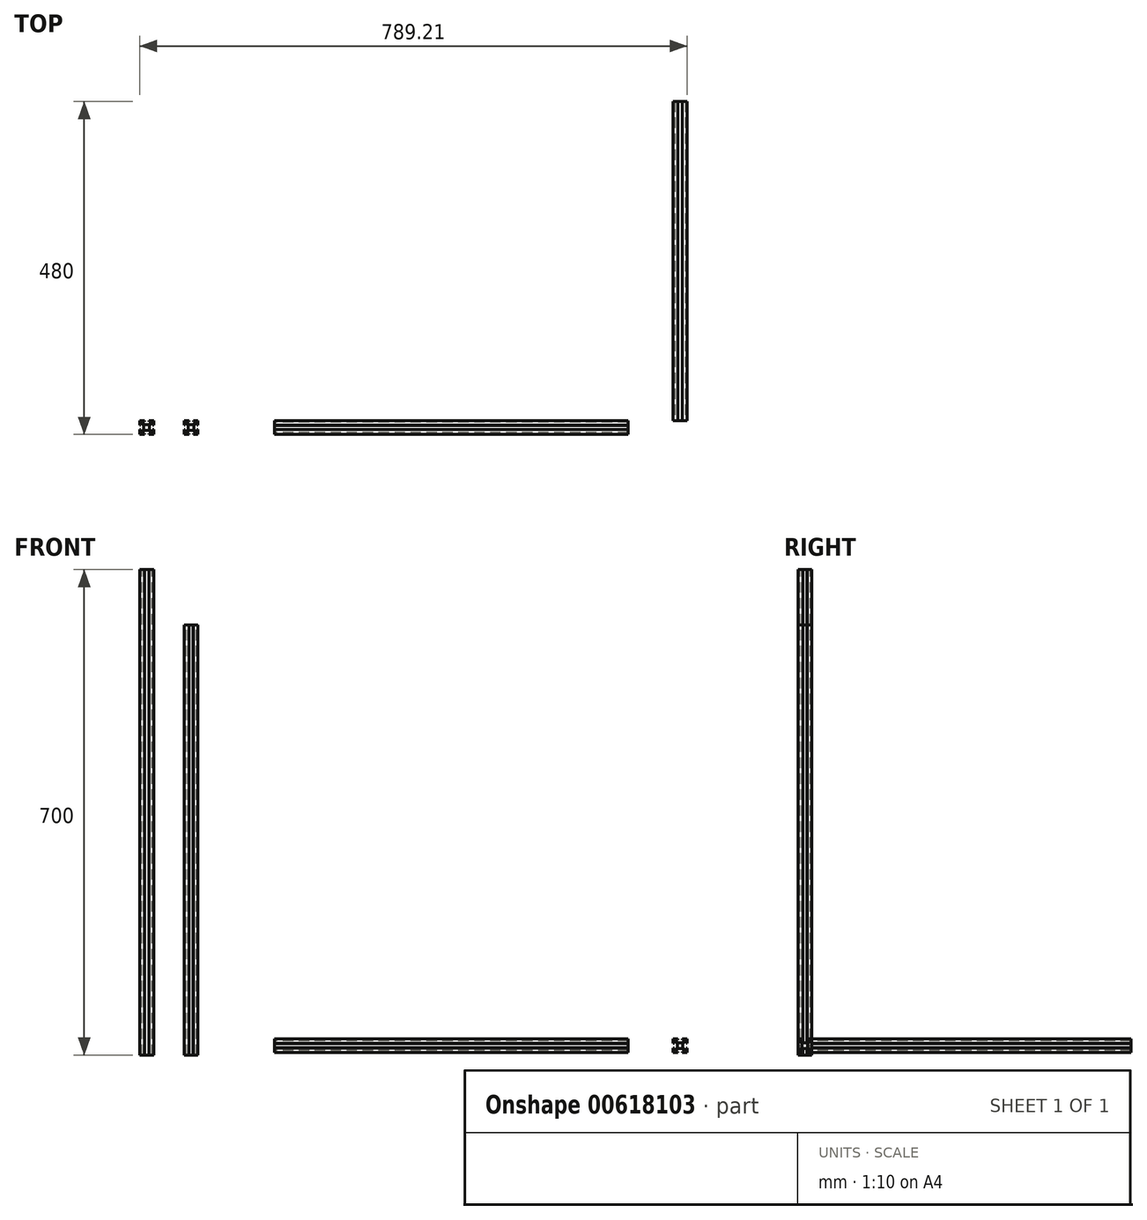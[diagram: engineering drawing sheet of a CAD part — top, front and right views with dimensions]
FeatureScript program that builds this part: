
annotation { "Feature Type Name" : "Feature", "Feature Type Description" : "" }
export const myFeature = defineFeature(function(context is Context, id is Id, definition is map)
    precondition{}
    {
        {
            var Q0;
            Q0=qCreatedBy(makeId("Front.planeOp"),FACE);
            var sketch = newSketch(context, id + "F0", { "sketchPlane" : qUnion([Q0])});
            skLineSegment(sketch, "E0.bottom", {"start": v(-64.1, 630.58) * mm, "end": v(-44.1, 630.58) * mm});
            skLineSegment(sketch, "E0.top", {"start": v(-64.1, -69.42) * mm, "end": v(-44.1, -69.42) * mm});
            skLineSegment(sketch, "E0.left", {"start": v(-64.1, 630.58) * mm, "end": v(-64.1, -69.42) * mm});
            skLineSegment(sketch, "E0.right", {"start": v(-44.1, 630.58) * mm, "end": v(-44.1, -69.42) * mm});
            skLineSegment(sketch, "E1.bottom", {"start": v(130.25, -46.02) * mm, "end": v(640.25, -46.02) * mm});
            skLineSegment(sketch, "E1.top", {"start": v(130.25, -66.02) * mm, "end": v(640.25, -66.02) * mm});
            skLineSegment(sketch, "E1.left", {"start": v(130.25, -46.02) * mm, "end": v(130.25, -66.02) * mm});
            skLineSegment(sketch, "E1.right", {"start": v(640.25, -46.02) * mm, "end": v(640.25, -66.02) * mm});
            skLineSegment(sketch, "E2.bottom", {"start": v(705.1, -66.02) * mm, "end": v(725.1, -66.02) * mm});
            skLineSegment(sketch, "E2.top", {"start": v(705.1, -46.02) * mm, "end": v(725.1, -46.02) * mm});
            skLineSegment(sketch, "E2.left", {"start": v(705.1, -66.02) * mm, "end": v(705.1, -46.02) * mm});
            skLineSegment(sketch, "E2.right", {"start": v(725.1, -66.02) * mm, "end": v(725.1, -46.02) * mm});
            skLineSegment(sketch, "E3.bottom", {"start": v(0, -69.42) * mm, "end": v(20, -69.42) * mm});
            skLineSegment(sketch, "E3.top", {"start": v(0, 550.58) * mm, "end": v(20, 550.58) * mm});
            skLineSegment(sketch, "E3.left", {"start": v(0, -69.42) * mm, "end": v(0, 550.58) * mm});
            skLineSegment(sketch, "E3.right", {"start": v(20, -69.42) * mm, "end": v(20, 550.58) * mm});
            skLineSegment(sketch, "E4.bottom", {"start": v(705.1, -46.02) * mm, "end": v(711.9, -46.02) * mm});
            skLineSegment(sketch, "E4.top", {"start": v(711.1, -56.02) * mm, "end": v(715.1, -56.02) * mm, "construction": true});
            skLineSegment(sketch, "E4.left", {"start": v(705.1, -46.02) * mm, "end": v(705.1, -52.82) * mm});
            skLineSegment(sketch, "E4.right", {"start": v(715.1, -52.02) * mm, "end": v(715.1, -56.02) * mm, "construction": true});
            skLineSegment(sketch, "E5", {"start": v(706.5, -48.41) * mm, "end": v(706.5, -52.82) * mm});
            skLineSegment(sketch, "E6", {"start": v(706.5, -52.82) * mm, "end": v(705.1, -52.82) * mm});
            skLineSegment(sketch, "E7", {"start": v(707.49, -47.42) * mm, "end": v(711.9, -47.42) * mm});
            skLineSegment(sketch, "E8", {"start": v(711.9, -47.42) * mm, "end": v(711.9, -46.02) * mm});
            skLineSegment(sketch, "E9", {"start": v(705.1, -46.02) * mm, "end": v(715.1, -56.02) * mm, "construction": true});
            skLineSegment(sketch, "E10", {"start": v(711.1, -53.01) * mm, "end": v(706.5, -48.41) * mm});
            skLineSegment(sketch, "E11", {"start": v(707.49, -47.42) * mm, "end": v(712.09, -52.02) * mm});
            skLineSegment(sketch, "E12", {"start": v(712.09, -52.02) * mm, "end": v(715.1, -52.02) * mm});
            skLineSegment(sketch, "E13", {"start": v(711.1, -53.01) * mm, "end": v(711.1, -56.02) * mm});
            skLineSegment(sketch, "E14.MirrorCS", {"start": v(722.7, -47.42) * mm, "end": v(718.1, -52.02) * mm});
            skLineSegment(sketch, "E15.MirrorCS", {"start": v(718.1, -52.02) * mm, "end": v(715.1, -52.02) * mm});
            skLineSegment(sketch, "E16.MirrorCS", {"start": v(719.1, -53.01) * mm, "end": v(719.1, -56.02) * mm});
            skLineSegment(sketch, "E17.MirrorCS", {"start": v(725.1, -46.02) * mm, "end": v(715.1, -56.02) * mm, "construction": true});
            skLineSegment(sketch, "E18.MirrorCS", {"start": v(719.1, -56.02) * mm, "end": v(715.1, -56.02) * mm, "construction": true});
            skLineSegment(sketch, "E19.MirrorCS", {"start": v(718.3, -47.42) * mm, "end": v(718.3, -46.02) * mm});
            skLineSegment(sketch, "E20.MirrorCS", {"start": v(719.1, -53.01) * mm, "end": v(723.7, -48.41) * mm});
            skLineSegment(sketch, "E21.MirrorCS", {"start": v(725.1, -46.02) * mm, "end": v(725.1, -52.82) * mm});
            skLineSegment(sketch, "E22.MirrorCS", {"start": v(723.7, -52.82) * mm, "end": v(725.1, -52.82) * mm});
            skLineSegment(sketch, "E23.MirrorCS", {"start": v(723.7, -48.41) * mm, "end": v(723.7, -52.82) * mm});
            skLineSegment(sketch, "E24.MirrorCS", {"start": v(725.1, -46.02) * mm, "end": v(718.3, -46.02) * mm});
            skLineSegment(sketch, "E25.MirrorCS", {"start": v(722.7, -47.42) * mm, "end": v(718.3, -47.42) * mm});
            skLineSegment(sketch, "E26.MirrorCS", {"start": v(725.1, -66.02) * mm, "end": v(725.1, -59.22) * mm});
            skLineSegment(sketch, "E27.MirrorCS", {"start": v(706.5, -63.63) * mm, "end": v(706.5, -59.22) * mm});
            skLineSegment(sketch, "E28.MirrorCS", {"start": v(711.1, -59.03) * mm, "end": v(711.1, -56.02) * mm});
            skLineSegment(sketch, "E29.MirrorCS", {"start": v(715.1, -60.02) * mm, "end": v(715.1, -56.02) * mm, "construction": true});
            skLineSegment(sketch, "E30.MirrorCS", {"start": v(723.7, -63.63) * mm, "end": v(723.7, -59.22) * mm});
            skLineSegment(sketch, "E31.MirrorCS", {"start": v(718.1, -60.02) * mm, "end": v(715.1, -60.02) * mm});
            skLineSegment(sketch, "E32.MirrorCS", {"start": v(718.3, -64.62) * mm, "end": v(718.3, -66.02) * mm});
            skLineSegment(sketch, "E33.MirrorCS", {"start": v(719.1, -59.03) * mm, "end": v(723.7, -63.63) * mm});
            skLineSegment(sketch, "E34.MirrorCS", {"start": v(705.1, -66.02) * mm, "end": v(715.1, -56.02) * mm, "construction": true});
            skLineSegment(sketch, "E35.MirrorCS", {"start": v(707.49, -64.62) * mm, "end": v(711.9, -64.62) * mm});
            skLineSegment(sketch, "E36.MirrorCS", {"start": v(722.7, -64.62) * mm, "end": v(718.3, -64.62) * mm});
            skLineSegment(sketch, "E37.MirrorCS", {"start": v(706.5, -59.22) * mm, "end": v(705.1, -59.22) * mm});
            skLineSegment(sketch, "E38.MirrorCS", {"start": v(705.1, -66.02) * mm, "end": v(711.9, -66.02) * mm});
            skLineSegment(sketch, "E39.MirrorCS", {"start": v(719.1, -59.03) * mm, "end": v(719.1, -56.02) * mm});
            skLineSegment(sketch, "E40.MirrorCS", {"start": v(707.49, -64.62) * mm, "end": v(712.09, -60.02) * mm});
            skLineSegment(sketch, "E41.MirrorCS", {"start": v(712.09, -60.02) * mm, "end": v(715.1, -60.02) * mm});
            skLineSegment(sketch, "E42.MirrorCS", {"start": v(705.1, -66.02) * mm, "end": v(705.1, -59.22) * mm});
            skLineSegment(sketch, "E43.MirrorCS", {"start": v(711.1, -59.03) * mm, "end": v(706.5, -63.63) * mm});
            skLineSegment(sketch, "E44.MirrorCS", {"start": v(725.1, -66.02) * mm, "end": v(715.1, -56.02) * mm, "construction": true});
            skLineSegment(sketch, "E45.MirrorCS", {"start": v(723.7, -59.22) * mm, "end": v(725.1, -59.22) * mm});
            skLineSegment(sketch, "E46.MirrorCS", {"start": v(722.7, -64.62) * mm, "end": v(718.1, -60.02) * mm});
            skLineSegment(sketch, "E47.MirrorCS", {"start": v(725.1, -66.02) * mm, "end": v(718.3, -66.02) * mm});
            skLineSegment(sketch, "E48.MirrorCS", {"start": v(711.9, -64.62) * mm, "end": v(711.9, -66.02) * mm});
            skLineSegment(sketch, "E49", {"start": v(711.9, -46.02) * mm, "end": v(718.3, -46.02) * mm});
            skLineSegment(sketch, "E50", {"start": v(725.1, -52.82) * mm, "end": v(725.1, -59.22) * mm});
            skLineSegment(sketch, "E51", {"start": v(718.3, -66.02) * mm, "end": v(711.9, -66.02) * mm});
            skLineSegment(sketch, "E52", {"start": v(705.1, -59.22) * mm, "end": v(705.1, -52.82) * mm});
            skSolve(sketch);
        }
        {
            var Q0;
            Q0=makeQuery(id+"F0.imprint","IMPRINT",FACE,{"disambiguationData":[TD([[makeQuery(id+"F0.imprint","IMPRINT",EDGE,{"derivedFrom":sQuery(id+"F0.wireOp",EDGE,"E0.bottom")}),-1.0]])]});
            var Q1;
            Q1=makeQuery(id+"F0.imprint","IMPRINT",FACE,{"disambiguationData":[TD([[makeQuery(id+"F0.imprint","IMPRINT",EDGE,{"derivedFrom":sQuery(id+"F0.wireOp",EDGE,"E1.bottom")}),-1.0]])]});
            var Q2;
            Q2=makeQuery(id+"F0.imprint","IMPRINT",FACE,{"disambiguationData":[TD([[makeQuery(id+"F0.imprint","IMPRINT",EDGE,{"derivedFrom":sQuery(id+"F0.wireOp",EDGE,"E3.bottom")}),1.0]])]});
            var Q3;
            Q3=makeQuery(id+"F0.imprint","IMPRINT",FACE,{"disambiguationData":[TD([[makeQuery(id+"F0.imprint","IMPRINT",EDGE,{"derivedFrom":sQuery(id+"F0.wireOp",EDGE,"fPh9Yb10-BMAz-MM7O-woml-nyBZ1UUOM5pv.bottom")}),-1.0]])]});
            extrude(context, id + "F1", {"entities" : qUnion([Q0, Q1, Q2, Q3]), "depth" : 20 * mm, "offsetDistance" : 25 * mm});
        }
        {
            var Q0;
            Q0=makeQuery(id+"F0.imprint","IMPRINT",FACE,{"disambiguationData":[TD([[makeQuery(id+"F0.imprint","IMPRINT",EDGE,{"derivedFrom":sQuery(id+"F0.wireOp",EDGE,"E2.bottom")}),1.0]])]});
            var Q1;
            Q1=makeQuery(id+"F0.imprint","IMPRINT",FACE,{"disambiguationData":[TD([[makeQuery(id+"F0.imprint","IMPRINT",EDGE,{"derivedFrom":sQuery(id+"F0.wireOp",EDGE,"E4.bottom")}),-1.0]])]});
            extrude(context, id + "F2", {"entities" : qUnion([Q0, Q1]), "oppositeDirection" : true, "depth" : 460 * mm, "offsetDistance" : 25 * mm});
        }
        {
            var Q0;
            Q0=makeQuery(id+"F1.opExtrude","SWEPT_FACE",FACE,{"disambiguationData":[OSD([sQuery(id+"F0.wireOp",EDGE,"E3.top")])]});
            var sketch = newSketch(context, id + "F3", { "sketchPlane" : qUnion([Q0])});
            skLineSegment(sketch, "E53.bottom", {"start": v(0, 0) * mm, "end": v(6.8, 0) * mm});
            skLineSegment(sketch, "E53.top", {"start": v(6, -10) * mm, "end": v(10, -10) * mm, "construction": true});
            skLineSegment(sketch, "E53.left", {"start": v(0, 0) * mm, "end": v(0, -6.8) * mm});
            skLineSegment(sketch, "E53.right", {"start": v(10, -6) * mm, "end": v(10, -10) * mm, "construction": true});
            skLineSegment(sketch, "E54", {"start": v(1.4, -2.39) * mm, "end": v(1.4, -6.8) * mm});
            skLineSegment(sketch, "E55", {"start": v(1.4, -6.8) * mm, "end": v(0, -6.8) * mm});
            skLineSegment(sketch, "E56", {"start": v(2.39, -1.4) * mm, "end": v(6.8, -1.4) * mm});
            skLineSegment(sketch, "E57", {"start": v(6.8, -1.4) * mm, "end": v(6.8, 0) * mm});
            skLineSegment(sketch, "E58", {"start": v(0, 0) * mm, "end": v(10, -10) * mm, "construction": true});
            skLineSegment(sketch, "E59", {"start": v(6, -6.99) * mm, "end": v(1.4, -2.39) * mm});
            skLineSegment(sketch, "E60", {"start": v(2.39, -1.4) * mm, "end": v(6.99, -6) * mm});
            skLineSegment(sketch, "E61", {"start": v(6.99, -6) * mm, "end": v(10, -6) * mm});
            skLineSegment(sketch, "E62", {"start": v(6, -6.99) * mm, "end": v(6, -10) * mm});
            skLineSegment(sketch, "E63.MirrorCS", {"start": v(17.61, -1.4) * mm, "end": v(13.01, -6) * mm});
            skLineSegment(sketch, "E64.MirrorCS", {"start": v(13.01, -6) * mm, "end": v(10, -6) * mm});
            skLineSegment(sketch, "E65.MirrorCS", {"start": v(14, -6.99) * mm, "end": v(14, -10) * mm});
            skLineSegment(sketch, "E66.MirrorCS", {"start": v(20, 0) * mm, "end": v(10, -10) * mm, "construction": true});
            skLineSegment(sketch, "E67.MirrorCS", {"start": v(14, -10) * mm, "end": v(10, -10) * mm, "construction": true});
            skLineSegment(sketch, "E68.MirrorCS", {"start": v(13.2, -1.4) * mm, "end": v(13.2, 0) * mm});
            skLineSegment(sketch, "E69.MirrorCS", {"start": v(14, -6.99) * mm, "end": v(18.6, -2.39) * mm});
            skLineSegment(sketch, "E70.MirrorCS", {"start": v(20, 0) * mm, "end": v(20, -6.8) * mm});
            skLineSegment(sketch, "E71.MirrorCS", {"start": v(18.6, -6.8) * mm, "end": v(20, -6.8) * mm});
            skLineSegment(sketch, "E72.MirrorCS", {"start": v(18.6, -2.39) * mm, "end": v(18.6, -6.8) * mm});
            skLineSegment(sketch, "E73.MirrorCS", {"start": v(20, 0) * mm, "end": v(13.2, 0) * mm});
            skLineSegment(sketch, "E74.MirrorCS", {"start": v(17.61, -1.4) * mm, "end": v(13.2, -1.4) * mm});
            skLineSegment(sketch, "E75.MirrorCS", {"start": v(20, -20) * mm, "end": v(20, -13.2) * mm});
            skLineSegment(sketch, "E76.MirrorCS", {"start": v(1.4, -17.61) * mm, "end": v(1.4, -13.2) * mm});
            skLineSegment(sketch, "E77.MirrorCS", {"start": v(6, -13.01) * mm, "end": v(6, -10) * mm});
            skLineSegment(sketch, "E78.MirrorCS", {"start": v(10, -14) * mm, "end": v(10, -10) * mm, "construction": true});
            skLineSegment(sketch, "E79.MirrorCS", {"start": v(18.6, -17.61) * mm, "end": v(18.6, -13.2) * mm});
            skLineSegment(sketch, "E80.MirrorCS", {"start": v(13.01, -14) * mm, "end": v(10, -14) * mm});
            skLineSegment(sketch, "E81.MirrorCS", {"start": v(13.2, -18.6) * mm, "end": v(13.2, -20) * mm});
            skLineSegment(sketch, "E82.MirrorCS", {"start": v(14, -13.01) * mm, "end": v(18.6, -17.61) * mm});
            skLineSegment(sketch, "E83.MirrorCS", {"start": v(0, -20) * mm, "end": v(10, -10) * mm, "construction": true});
            skLineSegment(sketch, "E84.MirrorCS", {"start": v(2.39, -18.6) * mm, "end": v(6.8, -18.6) * mm});
            skLineSegment(sketch, "E85.MirrorCS", {"start": v(17.61, -18.6) * mm, "end": v(13.2, -18.6) * mm});
            skLineSegment(sketch, "E86.MirrorCS", {"start": v(1.4, -13.2) * mm, "end": v(0, -13.2) * mm});
            skLineSegment(sketch, "E87.MirrorCS", {"start": v(0, -20) * mm, "end": v(6.8, -20) * mm});
            skLineSegment(sketch, "E88.MirrorCS", {"start": v(14, -13.01) * mm, "end": v(14, -10) * mm});
            skLineSegment(sketch, "E89.MirrorCS", {"start": v(2.39, -18.6) * mm, "end": v(6.99, -14) * mm});
            skLineSegment(sketch, "E90.MirrorCS", {"start": v(6.99, -14) * mm, "end": v(10, -14) * mm});
            skLineSegment(sketch, "E91.MirrorCS", {"start": v(0, -20) * mm, "end": v(0, -13.2) * mm});
            skLineSegment(sketch, "E92.MirrorCS", {"start": v(6, -13.01) * mm, "end": v(1.4, -17.61) * mm});
            skLineSegment(sketch, "E93.MirrorCS", {"start": v(20, -20) * mm, "end": v(10, -10) * mm, "construction": true});
            skLineSegment(sketch, "E94.MirrorCS", {"start": v(18.6, -13.2) * mm, "end": v(20, -13.2) * mm});
            skLineSegment(sketch, "E95.MirrorCS", {"start": v(17.61, -18.6) * mm, "end": v(13.01, -14) * mm});
            skLineSegment(sketch, "E96.MirrorCS", {"start": v(20, -20) * mm, "end": v(13.2, -20) * mm});
            skLineSegment(sketch, "E97.MirrorCS", {"start": v(6.8, -18.6) * mm, "end": v(6.8, -20) * mm});
            skLineSegment(sketch, "E98", {"start": v(6.8, 0) * mm, "end": v(13.2, 0) * mm});
            skLineSegment(sketch, "E99", {"start": v(20, -6.8) * mm, "end": v(20, -13.2) * mm});
            skLineSegment(sketch, "E100", {"start": v(13.2, -20) * mm, "end": v(6.8, -20) * mm});
            skLineSegment(sketch, "E101", {"start": v(0, -13.2) * mm, "end": v(0, -6.8) * mm});
            skSolve(sketch);
        }
        {
            var Q0;
            Q0=makeQuery(id+"F3.imprint","IMPRINT",FACE,{"disambiguationData":[TD([[makeQuery(id+"F3.imprint","IMPRINT",EDGE,{"derivedFrom":sQuery(id+"F3.wireOp",EDGE,"E56")}),-1.0]])]});
            var Q1;
            Q1=makeQuery(id+"F3.imprint","IMPRINT",FACE,{"disambiguationData":[TD([[makeQuery(id+"F3.imprint","IMPRINT",EDGE,{"derivedFrom":sQuery(id+"F3.wireOp",EDGE,"E65.MirrorCS")}),1.0]])]});
            var Q2;
            Q2=makeQuery(id+"F3.imprint","IMPRINT",FACE,{"disambiguationData":[TD([[makeQuery(id+"F3.imprint","IMPRINT",EDGE,{"derivedFrom":sQuery(id+"F3.wireOp",EDGE,"E80.MirrorCS")}),1.0]])]});
            var Q3;
            Q3=makeQuery(id+"F3.imprint","IMPRINT",FACE,{"disambiguationData":[TD([[makeQuery(id+"F3.imprint","IMPRINT",EDGE,{"derivedFrom":sQuery(id+"F3.wireOp",EDGE,"E54")}),1.0]])]});
            extrude(context, id + "F4", {"entities" : qUnion([Q0, Q1, Q2, Q3]), "operationType" : NewBodyOperationType.REMOVE, "endBound" : BoundingType.UP_TO_NEXT, "oppositeDirection" : true, "depth" : 25 * mm, "offsetDistance" : 25 * mm});
        }
        {
            var Q0;
            Q0=makeQuery(id+"F1.opExtrude","SWEPT_FACE",FACE,{"disambiguationData":[OSD([sQuery(id+"F0.wireOp",EDGE,"E0.bottom")])]});
            var sketch = newSketch(context, id + "F5", { "sketchPlane" : qUnion([Q0])});
            skLineSegment(sketch, "E102.bottom", {"start": v(-64.1, 0) * mm, "end": v(-57.3, 0) * mm});
            skLineSegment(sketch, "E102.top", {"start": v(-58.1, -10) * mm, "end": v(-54.1, -10) * mm, "construction": true});
            skLineSegment(sketch, "E102.left", {"start": v(-64.1, 0) * mm, "end": v(-64.1, -6.8) * mm});
            skLineSegment(sketch, "E102.right", {"start": v(-54.1, -6) * mm, "end": v(-54.1, -10) * mm, "construction": true});
            skLineSegment(sketch, "E103", {"start": v(-62.7, -2.39) * mm, "end": v(-62.7, -6.8) * mm});
            skLineSegment(sketch, "E104", {"start": v(-62.7, -6.8) * mm, "end": v(-64.1, -6.8) * mm});
            skLineSegment(sketch, "E105", {"start": v(-61.72, -1.4) * mm, "end": v(-57.3, -1.4) * mm});
            skLineSegment(sketch, "E106", {"start": v(-57.3, -1.4) * mm, "end": v(-57.3, 0) * mm});
            skLineSegment(sketch, "E107", {"start": v(-64.1, 0) * mm, "end": v(-54.1, -10) * mm, "construction": true});
            skLineSegment(sketch, "E108", {"start": v(-58.1, -6.99) * mm, "end": v(-62.7, -2.39) * mm});
            skLineSegment(sketch, "E109", {"start": v(-61.72, -1.4) * mm, "end": v(-57.12, -6) * mm});
            skLineSegment(sketch, "E110", {"start": v(-57.12, -6) * mm, "end": v(-54.1, -6) * mm});
            skLineSegment(sketch, "E111", {"start": v(-58.1, -6.99) * mm, "end": v(-58.1, -10) * mm});
            skLineSegment(sketch, "E112.MirrorCS", {"start": v(-46.5, -1.4) * mm, "end": v(-51.1, -6) * mm});
            skLineSegment(sketch, "E113.MirrorCS", {"start": v(-51.1, -6) * mm, "end": v(-54.1, -6) * mm});
            skLineSegment(sketch, "E114.MirrorCS", {"start": v(-50.1, -6.99) * mm, "end": v(-50.1, -10) * mm});
            skLineSegment(sketch, "E115.MirrorCS", {"start": v(-44.1, 0) * mm, "end": v(-54.1, -10) * mm, "construction": true});
            skLineSegment(sketch, "E116.MirrorCS", {"start": v(-50.1, -10) * mm, "end": v(-54.1, -10) * mm, "construction": true});
            skLineSegment(sketch, "E117.MirrorCS", {"start": v(-50.9, -1.4) * mm, "end": v(-50.9, 0) * mm});
            skLineSegment(sketch, "E118.MirrorCS", {"start": v(-50.1, -6.99) * mm, "end": v(-45.5, -2.39) * mm});
            skLineSegment(sketch, "E119.MirrorCS", {"start": v(-44.1, 0) * mm, "end": v(-44.1, -6.8) * mm});
            skLineSegment(sketch, "E120.MirrorCS", {"start": v(-45.5, -6.8) * mm, "end": v(-44.1, -6.8) * mm});
            skLineSegment(sketch, "E121.MirrorCS", {"start": v(-45.5, -2.39) * mm, "end": v(-45.5, -6.8) * mm});
            skLineSegment(sketch, "E122.MirrorCS", {"start": v(-44.1, 0) * mm, "end": v(-50.9, 0) * mm});
            skLineSegment(sketch, "E123.MirrorCS", {"start": v(-46.5, -1.4) * mm, "end": v(-50.9, -1.4) * mm});
            skLineSegment(sketch, "E124.MirrorCS", {"start": v(-44.1, -20) * mm, "end": v(-44.1, -13.2) * mm});
            skLineSegment(sketch, "E125.MirrorCS", {"start": v(-62.7, -17.61) * mm, "end": v(-62.7, -13.2) * mm});
            skLineSegment(sketch, "E126.MirrorCS", {"start": v(-58.1, -13.01) * mm, "end": v(-58.1, -10) * mm});
            skLineSegment(sketch, "E127.MirrorCS", {"start": v(-54.1, -14) * mm, "end": v(-54.1, -10) * mm, "construction": true});
            skLineSegment(sketch, "E128.MirrorCS", {"start": v(-45.5, -17.61) * mm, "end": v(-45.5, -13.2) * mm});
            skLineSegment(sketch, "E129.MirrorCS", {"start": v(-51.1, -14) * mm, "end": v(-54.1, -14) * mm});
            skLineSegment(sketch, "E130.MirrorCS", {"start": v(-50.9, -18.6) * mm, "end": v(-50.9, -20) * mm});
            skLineSegment(sketch, "E131.MirrorCS", {"start": v(-50.1, -13.01) * mm, "end": v(-45.5, -17.61) * mm});
            skLineSegment(sketch, "E132.MirrorCS", {"start": v(-64.1, -20) * mm, "end": v(-54.1, -10) * mm, "construction": true});
            skLineSegment(sketch, "E133.MirrorCS", {"start": v(-61.72, -18.6) * mm, "end": v(-57.3, -18.6) * mm});
            skLineSegment(sketch, "E134.MirrorCS", {"start": v(-46.5, -18.6) * mm, "end": v(-50.9, -18.6) * mm});
            skLineSegment(sketch, "E135.MirrorCS", {"start": v(-62.7, -13.2) * mm, "end": v(-64.1, -13.2) * mm});
            skLineSegment(sketch, "E136.MirrorCS", {"start": v(-64.1, -20) * mm, "end": v(-57.3, -20) * mm});
            skLineSegment(sketch, "E137.MirrorCS", {"start": v(-50.1, -13.01) * mm, "end": v(-50.1, -10) * mm});
            skLineSegment(sketch, "E138.MirrorCS", {"start": v(-61.72, -18.6) * mm, "end": v(-57.12, -14) * mm});
            skLineSegment(sketch, "E139.MirrorCS", {"start": v(-57.12, -14) * mm, "end": v(-54.1, -14) * mm});
            skLineSegment(sketch, "E140.MirrorCS", {"start": v(-64.1, -20) * mm, "end": v(-64.1, -13.2) * mm});
            skLineSegment(sketch, "E141.MirrorCS", {"start": v(-58.1, -13.01) * mm, "end": v(-62.7, -17.61) * mm});
            skLineSegment(sketch, "E142.MirrorCS", {"start": v(-44.1, -20) * mm, "end": v(-54.1, -10) * mm, "construction": true});
            skLineSegment(sketch, "E143.MirrorCS", {"start": v(-45.5, -13.2) * mm, "end": v(-44.1, -13.2) * mm});
            skLineSegment(sketch, "E144.MirrorCS", {"start": v(-46.5, -18.6) * mm, "end": v(-51.1, -14) * mm});
            skLineSegment(sketch, "E145.MirrorCS", {"start": v(-44.1, -20) * mm, "end": v(-50.9, -20) * mm});
            skLineSegment(sketch, "E146.MirrorCS", {"start": v(-57.3, -18.6) * mm, "end": v(-57.3, -20) * mm});
            skLineSegment(sketch, "E147", {"start": v(-57.3, 0) * mm, "end": v(-50.9, 0) * mm});
            skLineSegment(sketch, "E148", {"start": v(-44.1, -6.8) * mm, "end": v(-44.1, -13.2) * mm});
            skLineSegment(sketch, "E149", {"start": v(-50.9, -20) * mm, "end": v(-57.3, -20) * mm});
            skLineSegment(sketch, "E150", {"start": v(-64.1, -13.2) * mm, "end": v(-64.1, -6.8) * mm});
            skPoint(sketch, "E151.0", {"position": v(-64.1, 0) * mm});
            skSolve(sketch);
        }
        {
            var Q0;
            Q0=makeQuery(id+"F5.imprint","IMPRINT",FACE,{"disambiguationData":[TD([[makeQuery(id+"F5.imprint","IMPRINT",EDGE,{"derivedFrom":sQuery(id+"F5.wireOp",EDGE,"E103")}),1.0]])]});
            var Q1;
            Q1=makeQuery(id+"F5.imprint","IMPRINT",FACE,{"disambiguationData":[TD([[makeQuery(id+"F5.imprint","IMPRINT",EDGE,{"derivedFrom":sQuery(id+"F5.wireOp",EDGE,"E105")}),-1.0]])]});
            var Q2;
            Q2=makeQuery(id+"F5.imprint","IMPRINT",FACE,{"disambiguationData":[TD([[makeQuery(id+"F5.imprint","IMPRINT",EDGE,{"derivedFrom":sQuery(id+"F5.wireOp",EDGE,"E114.MirrorCS")}),1.0]])]});
            var Q3;
            Q3=makeQuery(id+"F5.imprint","IMPRINT",FACE,{"disambiguationData":[TD([[makeQuery(id+"F5.imprint","IMPRINT",EDGE,{"derivedFrom":sQuery(id+"F5.wireOp",EDGE,"E129.MirrorCS")}),1.0]])]});
            extrude(context, id + "F6", {"entities" : qUnion([Q0, Q1, Q2, Q3]), "operationType" : NewBodyOperationType.REMOVE, "endBound" : BoundingType.UP_TO_NEXT, "oppositeDirection" : true, "depth" : 25 * mm, "offsetDistance" : 25 * mm});
        }
        {
            var Q0;
            Q0=makeQuery(id+"F1.opExtrude","SWEPT_FACE",FACE,{"disambiguationData":[OSD([sQuery(id+"F0.wireOp",EDGE,"E1.left")])]});
            var sketch = newSketch(context, id + "F7", { "sketchPlane" : qUnion([Q0])});
            skLineSegment(sketch, "E152.bottom", {"start": v(0, -46.02) * mm, "end": v(6.8, -46.02) * mm});
            skLineSegment(sketch, "E152.top", {"start": v(6, -56.02) * mm, "end": v(10, -56.02) * mm, "construction": true});
            skLineSegment(sketch, "E152.left", {"start": v(0, -46.02) * mm, "end": v(0, -52.82) * mm});
            skLineSegment(sketch, "E152.right", {"start": v(10, -52.02) * mm, "end": v(10, -56.02) * mm, "construction": true});
            skLineSegment(sketch, "E153", {"start": v(1.4, -48.41) * mm, "end": v(1.4, -52.82) * mm});
            skLineSegment(sketch, "E154", {"start": v(1.4, -52.82) * mm, "end": v(0, -52.82) * mm});
            skLineSegment(sketch, "E155", {"start": v(2.39, -47.42) * mm, "end": v(6.8, -47.42) * mm});
            skLineSegment(sketch, "E156", {"start": v(6.8, -47.42) * mm, "end": v(6.8, -46.02) * mm});
            skLineSegment(sketch, "E157", {"start": v(0, -46.02) * mm, "end": v(10, -56.02) * mm, "construction": true});
            skLineSegment(sketch, "E158", {"start": v(6, -53.01) * mm, "end": v(1.4, -48.41) * mm});
            skLineSegment(sketch, "E159", {"start": v(2.39, -47.42) * mm, "end": v(6.99, -52.02) * mm});
            skLineSegment(sketch, "E160", {"start": v(6.99, -52.02) * mm, "end": v(10, -52.02) * mm});
            skLineSegment(sketch, "E161", {"start": v(6, -53.01) * mm, "end": v(6, -56.02) * mm});
            skLineSegment(sketch, "E162.MirrorCS", {"start": v(17.61, -47.42) * mm, "end": v(13.01, -52.02) * mm});
            skLineSegment(sketch, "E163.MirrorCS", {"start": v(13.01, -52.02) * mm, "end": v(10, -52.02) * mm});
            skLineSegment(sketch, "E164.MirrorCS", {"start": v(14, -53.01) * mm, "end": v(14, -56.02) * mm});
            skLineSegment(sketch, "E165.MirrorCS", {"start": v(20, -46.02) * mm, "end": v(10, -56.02) * mm, "construction": true});
            skLineSegment(sketch, "E166.MirrorCS", {"start": v(14, -56.02) * mm, "end": v(10, -56.02) * mm, "construction": true});
            skLineSegment(sketch, "E167.MirrorCS", {"start": v(13.2, -47.42) * mm, "end": v(13.2, -46.02) * mm});
            skLineSegment(sketch, "E168.MirrorCS", {"start": v(14, -53.01) * mm, "end": v(18.6, -48.41) * mm});
            skLineSegment(sketch, "E169.MirrorCS", {"start": v(20, -46.02) * mm, "end": v(20, -52.82) * mm});
            skLineSegment(sketch, "E170.MirrorCS", {"start": v(18.6, -52.82) * mm, "end": v(20, -52.82) * mm});
            skLineSegment(sketch, "E171.MirrorCS", {"start": v(18.6, -48.41) * mm, "end": v(18.6, -52.82) * mm});
            skLineSegment(sketch, "E172.MirrorCS", {"start": v(20, -46.02) * mm, "end": v(13.2, -46.02) * mm});
            skLineSegment(sketch, "E173.MirrorCS", {"start": v(17.61, -47.42) * mm, "end": v(13.2, -47.42) * mm});
            skLineSegment(sketch, "E174.MirrorCS", {"start": v(20, -66.02) * mm, "end": v(20, -59.22) * mm});
            skLineSegment(sketch, "E175.MirrorCS", {"start": v(1.4, -63.63) * mm, "end": v(1.4, -59.22) * mm});
            skLineSegment(sketch, "E176.MirrorCS", {"start": v(6, -59.03) * mm, "end": v(6, -56.02) * mm});
            skLineSegment(sketch, "E177.MirrorCS", {"start": v(10, -60.02) * mm, "end": v(10, -56.02) * mm, "construction": true});
            skLineSegment(sketch, "E178.MirrorCS", {"start": v(18.6, -63.63) * mm, "end": v(18.6, -59.22) * mm});
            skLineSegment(sketch, "E179.MirrorCS", {"start": v(13.01, -60.02) * mm, "end": v(10, -60.02) * mm});
            skLineSegment(sketch, "E180.MirrorCS", {"start": v(13.2, -64.62) * mm, "end": v(13.2, -66.02) * mm});
            skLineSegment(sketch, "E181.MirrorCS", {"start": v(14, -59.03) * mm, "end": v(18.6, -63.63) * mm});
            skLineSegment(sketch, "E182.MirrorCS", {"start": v(0, -66.02) * mm, "end": v(10, -56.02) * mm, "construction": true});
            skLineSegment(sketch, "E183.MirrorCS", {"start": v(2.39, -64.62) * mm, "end": v(6.8, -64.62) * mm});
            skLineSegment(sketch, "E184.MirrorCS", {"start": v(17.61, -64.62) * mm, "end": v(13.2, -64.62) * mm});
            skLineSegment(sketch, "E185.MirrorCS", {"start": v(1.4, -59.22) * mm, "end": v(0, -59.22) * mm});
            skLineSegment(sketch, "E186.MirrorCS", {"start": v(0, -66.02) * mm, "end": v(6.8, -66.02) * mm});
            skLineSegment(sketch, "E187.MirrorCS", {"start": v(14, -59.03) * mm, "end": v(14, -56.02) * mm});
            skLineSegment(sketch, "E188.MirrorCS", {"start": v(2.39, -64.62) * mm, "end": v(6.99, -60.02) * mm});
            skLineSegment(sketch, "E189.MirrorCS", {"start": v(6.99, -60.02) * mm, "end": v(10, -60.02) * mm});
            skLineSegment(sketch, "E190.MirrorCS", {"start": v(0, -66.02) * mm, "end": v(0, -59.22) * mm});
            skLineSegment(sketch, "E191.MirrorCS", {"start": v(6, -59.03) * mm, "end": v(1.4, -63.63) * mm});
            skLineSegment(sketch, "E192.MirrorCS", {"start": v(20, -66.02) * mm, "end": v(10, -56.02) * mm, "construction": true});
            skLineSegment(sketch, "E193.MirrorCS", {"start": v(18.6, -59.22) * mm, "end": v(20, -59.22) * mm});
            skLineSegment(sketch, "E194.MirrorCS", {"start": v(17.61, -64.62) * mm, "end": v(13.01, -60.02) * mm});
            skLineSegment(sketch, "E195.MirrorCS", {"start": v(20, -66.02) * mm, "end": v(13.2, -66.02) * mm});
            skLineSegment(sketch, "E196.MirrorCS", {"start": v(6.8, -64.62) * mm, "end": v(6.8, -66.02) * mm});
            skLineSegment(sketch, "E197", {"start": v(6.8, -46.02) * mm, "end": v(13.2, -46.02) * mm});
            skLineSegment(sketch, "E198", {"start": v(20, -52.82) * mm, "end": v(20, -59.22) * mm});
            skLineSegment(sketch, "E199", {"start": v(13.2, -66.02) * mm, "end": v(6.8, -66.02) * mm});
            skLineSegment(sketch, "E200", {"start": v(0, -59.22) * mm, "end": v(0, -52.82) * mm});
            skSolve(sketch);
        }
        {
            var Q0;
            Q0=makeQuery(id+"F7.imprint","IMPRINT",FACE,{"disambiguationData":[TD([[makeQuery(id+"F7.imprint","IMPRINT",EDGE,{"derivedFrom":sQuery(id+"F7.wireOp",EDGE,"E155")}),-1.0]])]});
            var Q1;
            Q1=makeQuery(id+"F7.imprint","IMPRINT",FACE,{"disambiguationData":[TD([[makeQuery(id+"F7.imprint","IMPRINT",EDGE,{"derivedFrom":sQuery(id+"F7.wireOp",EDGE,"E164.MirrorCS")}),1.0]])]});
            var Q2;
            Q2=makeQuery(id+"F7.imprint","IMPRINT",FACE,{"disambiguationData":[TD([[makeQuery(id+"F7.imprint","IMPRINT",EDGE,{"derivedFrom":sQuery(id+"F7.wireOp",EDGE,"E179.MirrorCS")}),1.0]])]});
            var Q3;
            Q3=makeQuery(id+"F7.imprint","IMPRINT",FACE,{"disambiguationData":[TD([[makeQuery(id+"F7.imprint","IMPRINT",EDGE,{"derivedFrom":sQuery(id+"F7.wireOp",EDGE,"E153")}),1.0]])]});
            extrude(context, id + "F8", {"entities" : qUnion([Q0, Q1, Q2, Q3]), "operationType" : NewBodyOperationType.REMOVE, "endBound" : BoundingType.UP_TO_NEXT, "oppositeDirection" : true, "depth" : 25 * mm, "offsetDistance" : 25 * mm});
        }
    });
